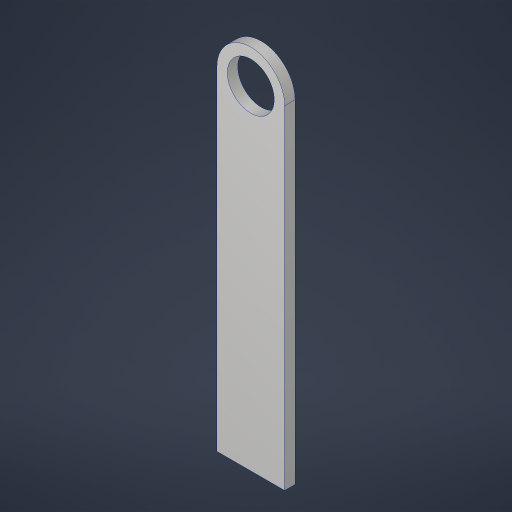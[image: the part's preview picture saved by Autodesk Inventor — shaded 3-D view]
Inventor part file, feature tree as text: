
AUTODESK INVENTOR PART (.ipt)
format: ipt  version: 2023.4 (Build 274418000, 418)  size: 171,008 bytes
history: native  units: in
note: dims shown in document units (in); Inventor stores cm internally (conversion verified against a paired STEP export)
features: extrude x1, sketch x1
ambient origin geometry x8: Origin, YZ Plane, XZ Plane, XY Plane, X Axis, Y Axis, Z Axis, Center Point
bodies: Solid1 (feature_tree)
feature tree (2):
  extrude  "Extrusion1"  Depth=0.25in
  sketch  "Sketch1"  dims[d0=1.125in d1=0.25in d2=8.0in d3=0.25in d4=0.0in]
